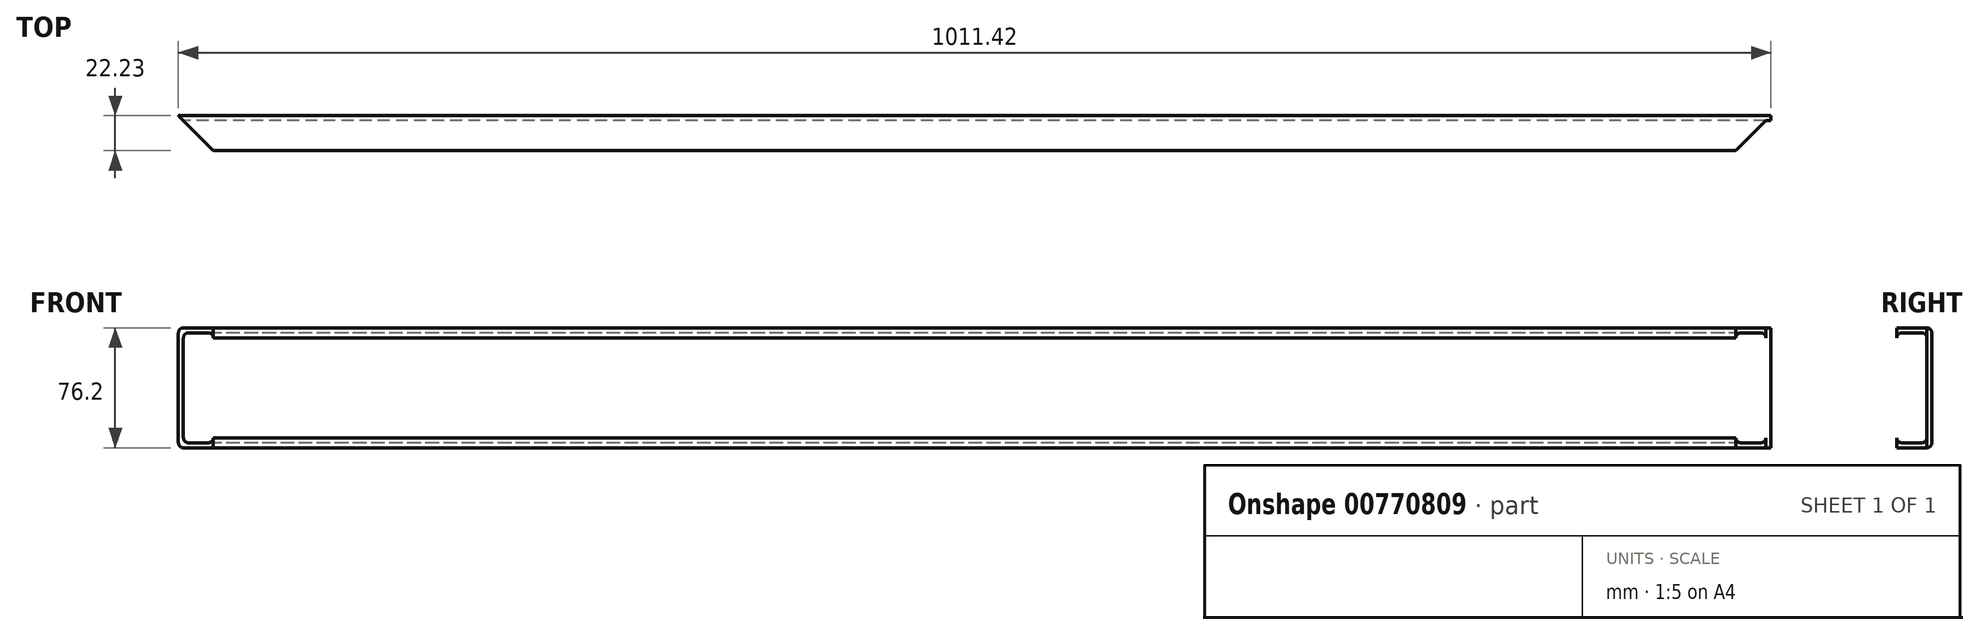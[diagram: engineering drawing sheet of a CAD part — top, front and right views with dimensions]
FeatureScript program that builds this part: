
annotation { "Feature Type Name" : "Feature", "Feature Type Description" : "" }
export const myFeature = defineFeature(function(context is Context, id is Id, definition is map)
    precondition{}
    {
        {
            var Q0;
            Q0=qCreatedBy(makeId("Right.planeOp"),FACE);
            var sketch = newSketch(context, id + "F0", { "sketchPlane" : qUnion([Q0])});
            skLineSegment(sketch, "E0.bottom", {"start": v(3.18, 0) * mm, "end": v(22.23, 0) * mm});
            skLineSegment(sketch, "E0.top", {"start": v(3.18, 76.2) * mm, "end": v(22.22, 76.2) * mm});
            skLineSegment(sketch, "E0.left", {"start": v(0, 3.18) * mm, "end": v(0, 73.03) * mm});
            skLineSegment(sketch, "E0.right", {"start": v(25.4, 3.18) * mm, "end": v(25.4, 73.03) * mm});
            skLineSegment(sketch, "E1.bottom", {"start": v(6.35, 3.18) * mm, "end": v(19.05, 3.18) * mm});
            skLineSegment(sketch, "E1.top", {"start": v(6.35, 73.03) * mm, "end": v(19.05, 73.03) * mm});
            skLineSegment(sketch, "E1.left", {"start": v(3.18, 6.35) * mm, "end": v(3.18, 69.85) * mm});
            skLineSegment(sketch, "E1.right", {"start": v(22.22, 6.35) * mm, "end": v(22.22, 69.85) * mm});
            skPoint(sketch, "E2.visualSharp", {"position": v(25.4, 76.2) * mm});
            skArc(sketch, "E2.filletArc", {"start": v(25.4, 73.03) * mm, "mid": v(24.47, 75.27) * mm, "end": v(22.22, 76.2) * mm});
            skPoint(sketch, "E3.visualSharp", {"position": v(25.4, 0) * mm});
            skArc(sketch, "E3.filletArc", {"start": v(22.23, 0) * mm, "mid": v(24.47, 0.93) * mm, "end": v(25.4, 3.18) * mm});
            skPoint(sketch, "E4.visualSharp", {"position": v(22.23, 3.18) * mm});
            skArc(sketch, "E4.filletArc", {"start": v(19.05, 3.18) * mm, "mid": v(21.3, 4.1) * mm, "end": v(22.22, 6.35) * mm});
            skPoint(sketch, "E5.visualSharp", {"position": v(3.18, 3.18) * mm});
            skArc(sketch, "E5.filletArc", {"start": v(3.18, 6.35) * mm, "mid": v(4.1, 4.1) * mm, "end": v(6.35, 3.18) * mm});
            skPoint(sketch, "E6.visualSharp", {"position": v(0, 0) * mm});
            skArc(sketch, "E6.filletArc", {"start": v(0, 3.18) * mm, "mid": v(0.93, 0.93) * mm, "end": v(3.18, 0) * mm});
            skPoint(sketch, "E7.visualSharp", {"position": v(3.18, 73.03) * mm});
            skArc(sketch, "E7.filletArc", {"start": v(6.35, 73.03) * mm, "mid": v(4.1, 72.1) * mm, "end": v(3.17, 69.85) * mm});
            skPoint(sketch, "E8.visualSharp", {"position": v(0, 76.2) * mm});
            skArc(sketch, "E8.filletArc", {"start": v(3.17, 76.2) * mm, "mid": v(0.93, 75.27) * mm, "end": v(0, 73.03) * mm});
            skArc(sketch, "E9.filletArc", {"start": v(22.22, 69.85) * mm, "mid": v(21.3, 72.1) * mm, "end": v(19.05, 73.03) * mm});
            skSolve(sketch);
        }
        {
            var Q0;
            Q0=makeQuery(id+"F0.imprint","IMPRINT",FACE,{"disambiguationData":[TD([[makeQuery(id+"F0.imprint","IMPRINT",EDGE,{"derivedFrom":sQuery(id+"F0.wireOp",EDGE,"E0.bottom")}),1.0]])]});
            extrude(context, id + "F1", {"entities" : qUnion([Q0]), "depth" : 1011.43 * mm, "offsetDistance" : 25.4 * mm});
        }
        {
            var Q0;
            Q0=makeQuery(id+"F1.opExtrude","SWEPT_FACE",FACE,{"disambiguationData":[OSD([sQuery(id+"F0.wireOp",EDGE,"E0.bottom")])]});
            var sketch = newSketch(context, id + "F2", { "sketchPlane" : qUnion([Q0])});
            skLineSegment(sketch, "E10", {"start": v(0, 0) * mm, "end": v(25.4, 0) * mm});
            skLineSegment(sketch, "E11", {"start": v(25.4, 0) * mm, "end": v(0, -25.4) * mm});
            skLineSegment(sketch, "E12", {"start": v(0, -25.4) * mm, "end": v(0, 0) * mm});
            skSolve(sketch);
        }
        {
            var Q0;
            {var subQ0=sQuery(id+"F2.wireOp",EDGE,"E11");var subQ1=sQuery(id+"F0.wireOp",EDGE,"E0.bottom");var subQ2=makeQuery(id+"F1.opExtrude","SWEPT_EDGE",EDGE,{"disambiguationData":[OSD([subQ1,sQuery(id+"F0.wireOp",EDGE,"E6.filletArc")])]});var subQ3=makeQuery(id+"F2.imprint","INTERSECT",VERTEX,{"derivedFrom":[subQ2,subQ0]});Q0=makeQuery(id+"F2.imprint","IMPRINT",FACE,{"disambiguationData":[TD([[makeQuery(id+"F2.imprint","IMPRINT",EDGE,{"disambiguationData":[TD([[subQ3,-1.0]])],"derivedFrom":subQ0}),-1.0]])]});}
            var Q1;
            {var subQ0=sQuery(id+"F2.wireOp",EDGE,"E12");var subQ1=sQuery(id+"F2.wireOp",EDGE,"E11");var subQ2=makeQuery(id+"F2.imprint","INTERSECT",VERTEX,{"derivedFrom":[subQ1,subQ0]});Q1=makeQuery(id+"F2.imprint","IMPRINT",FACE,{"disambiguationData":[TD([[makeQuery(id+"F2.imprint","IMPRINT",EDGE,{"disambiguationData":[TD([[subQ2,1.0]])],"derivedFrom":subQ1}),-1.0]])]});}
            var Q2;
            {var subQ0=sQuery(id+"F2.wireOp",EDGE,"E10");Q2=makeQuery(id+"F2.imprint","IMPRINT",FACE,{"disambiguationData":[TD([[makeQuery(id+"F2.imprint","IMPRINT",EDGE,{"derivedFrom":subQ0}),-1.0]])]});}
            extrude(context, id + "F3", {"entities" : qUnion([Q0, Q1, Q2]), "operationType" : NewBodyOperationType.REMOVE, "endBound" : BoundingType.THROUGH_ALL, "oppositeDirection" : true, "depth" : 25.4 * mm, "offsetDistance" : 25.4 * mm});
        }
        {
            var Q0;
            Q0=makeQuery(id+"F1.opExtrude","SWEPT_FACE",FACE,{"disambiguationData":[OSD([sQuery(id+"F0.wireOp",EDGE,"E0.top")])]});
            var sketch = newSketch(context, id + "F4", { "sketchPlane" : qUnion([Q0])});
            skLineSegment(sketch, "E13.0", {"start": v(1011.43, 25.4) * mm, "end": v(0, 25.4) * mm});
            skLineSegment(sketch, "E14.0", {"start": v(1011.43, 25.4) * mm, "end": v(1011.43, 22.22) * mm});
            skLineSegment(sketch, "E15.0.0", {"start": v(22.23, 3.17) * mm, "end": v(25.4, 0) * mm});
            skLineSegment(sketch, "E15.0.1", {"start": v(25.4, 0) * mm, "end": v(1011.43, 0) * mm});
            skLineSegment(sketch, "E15.0.2", {"start": v(1011.43, 0) * mm, "end": v(1011.43, 3.17) * mm});
            skLineSegment(sketch, "E15.0.3", {"start": v(1011.43, 3.17) * mm, "end": v(22.23, 3.17) * mm});
            skLineSegment(sketch, "E16", {"start": v(1011.43, 25.4) * mm, "end": v(1011.43, 0) * mm});
            skLineSegment(sketch, "E17", {"start": v(986.03, 0) * mm, "end": v(1011.43, 25.4) * mm});
            skSolve(sketch);
        }
        {
            var Q0;
            {var subQ0=sQuery(id+"F4.wireOp",EDGE,"E16");var subQ1=makeQuery(id+"F1.opExtrude","SWEPT_EDGE",EDGE,{"disambiguationData":[OSD([sQuery(id+"F0.wireOp",EDGE,"E0.top"),sQuery(id+"F0.wireOp",EDGE,"E2.filletArc")])]});var subQ2=makeQuery(id+"F4.imprint","INTERSECT",VERTEX,{"derivedFrom":[subQ1,subQ0]});var subQ3=sQuery(id+"F4.wireOp",EDGE,"E17");var subQ4=makeQuery(id+"F4.imprint","INTERSECT",VERTEX,{"derivedFrom":[subQ0,subQ3]});Q0=makeQuery(id+"F4.imprint","IMPRINT",FACE,{"disambiguationData":[TD([[makeQuery(id+"F4.imprint","IMPRINT",EDGE,{"disambiguationData":[TD([[subQ2,1.0],[subQ4,-1.0]])],"derivedFrom":subQ0}),-1.0]])]});}
            var Q1;
            {var subQ0=sQuery(id+"F4.wireOp",EDGE,"E16");var subQ1=sQuery(id+"F4.wireOp",EDGE,"E15.0.1");var subQ2=makeQuery(id+"F4.imprint","INTERSECT",VERTEX,{"derivedFrom":[subQ1,subQ0]});Q1=makeQuery(id+"F4.imprint","IMPRINT",FACE,{"disambiguationData":[TD([[makeQuery(id+"F4.imprint","IMPRINT",EDGE,{"disambiguationData":[TD([[subQ2,1.0]])],"derivedFrom":subQ1}),1.0]])]});}
            var Q2;
            {var subQ0=sQuery(id+"F4.wireOp",EDGE,"E16");var subQ1=sQuery(id+"F4.wireOp",EDGE,"E15.0.3");var subQ2=makeQuery(id+"F4.imprint","INTERSECT",VERTEX,{"derivedFrom":[subQ1,subQ0]});Q2=makeQuery(id+"F4.imprint","IMPRINT",FACE,{"disambiguationData":[TD([[makeQuery(id+"F4.imprint","IMPRINT",EDGE,{"disambiguationData":[TD([[subQ2,-1.0]])],"derivedFrom":subQ1}),-1.0]])]});}
            extrude(context, id + "F5", {"entities" : qUnion([Q0, Q1, Q2]), "operationType" : NewBodyOperationType.REMOVE, "endBound" : BoundingType.THROUGH_ALL, "oppositeDirection" : true, "depth" : 25.4 * mm, "offsetDistance" : 25.4 * mm});
        }
    });
